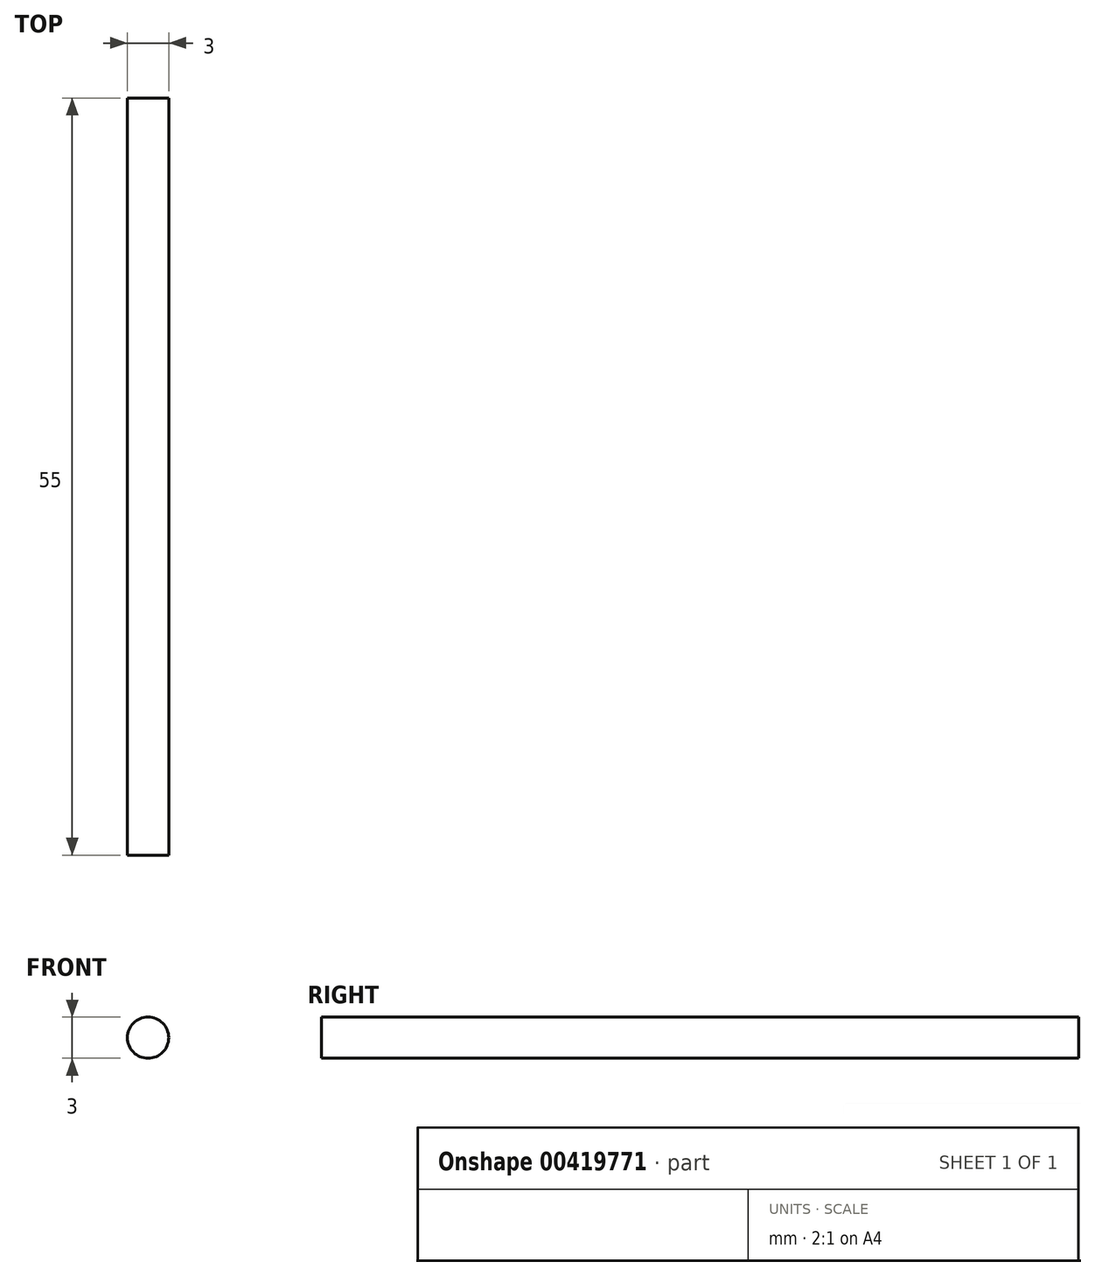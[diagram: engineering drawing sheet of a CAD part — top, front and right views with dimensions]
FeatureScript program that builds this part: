
annotation { "Feature Type Name" : "Feature", "Feature Type Description" : "" }
export const myFeature = defineFeature(function(context is Context, id is Id, definition is map)
    precondition{}
    {
        {
            var Q0;
            Q0=qCreatedBy(makeId("Front.planeOp"),FACE);
            var sketch = newSketch(context, id + "F0", { "sketchPlane" : qUnion([Q0])});
            skCircle(sketch, "E0", {"center": v(0, 0) * mm, "radius": 1.5 * mm});
            skSolve(sketch);
        }
        {
            var Q0;
            Q0=makeQuery(id+"F0.imprint","IMPRINT",FACE,{"disambiguationData":[TD([[makeQuery(id+"F0.imprint","IMPRINT",EDGE,{"derivedFrom":sQuery(id+"F0.wireOp",EDGE,"E0")}),1.0]])]});
            extrude(context, id + "F1", {"entities" : qUnion([Q0]), "depth" : 55 * mm});
        }
    });
